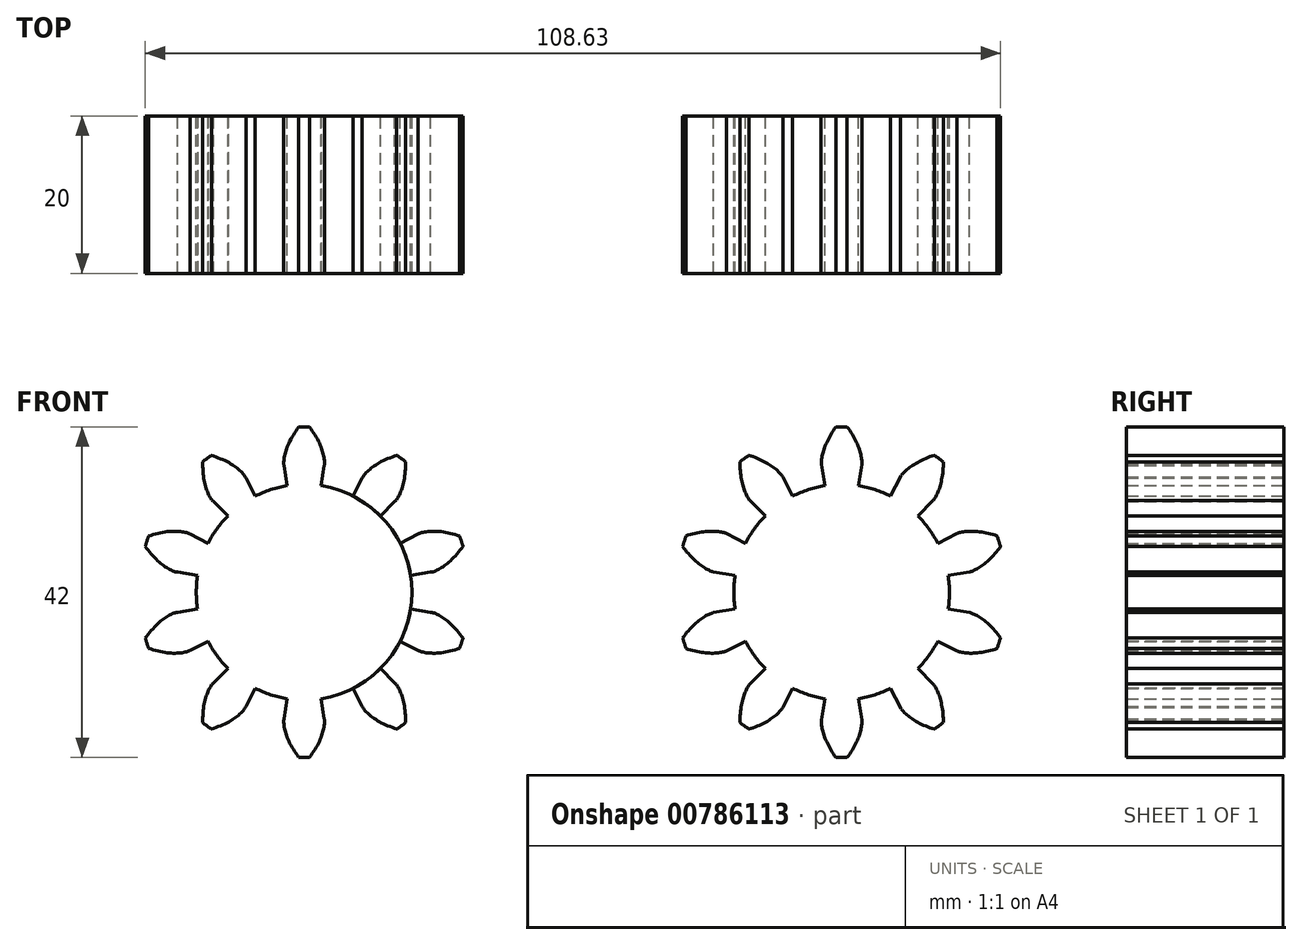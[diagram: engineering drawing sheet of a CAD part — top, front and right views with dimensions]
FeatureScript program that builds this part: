
annotation { "Feature Type Name" : "Feature", "Feature Type Description" : "" }
export const myFeature = defineFeature(function(context is Context, id is Id, definition is map)
    precondition{}
    {
        {
            var Q0;
            Q0=qCreatedBy(makeId("Front.planeOp"),FACE);
            var sketch = newSketch(context, id + "F0", { "sketchPlane" : qUnion([Q0])});
            skPoint(sketch, "E0.orphan", {"position": v(0, 0) * mm});
            skArc(sketch, "E1.0", {"start": v(0.7, 20.99) * mm, "mid": v(0, 21) * mm, "end": v(-0.7, 20.99) * mm});
            skArc(sketch, "E2.0", {"start": v(2.14, 13.53) * mm, "mid": v(0, 13.7) * mm, "end": v(-2.14, 13.53) * mm});
            skLineSegment(sketch, "E3", {"start": v(-2.14, 13.53) * mm, "end": v(-2.57, 16.24) * mm});
            skFitSpline(sketch, "E4", {"points": [v(-2.57, 16.24) * mm, v(-2.58, 16.45) * mm, v(-2.52, 17.07) * mm, v(-2.27, 18.07) * mm, v(-1.7, 19.4) * mm, v(-0.7, 20.99) * mm], "startDerivative": vector(-0.4, 1.4) * mm, "endDerivative": vector(3.94, 4.8) * mm});
            skLineSegment(sketch, "E5", {"start": v(-14.7, 0) * mm, "end": v(38.97, 0) * mm, "construction": true});
            skFitSpline(sketch, "E6.MirrorCS", {"points": [v(2.57, 16.24) * mm, v(2.58, 16.45) * mm, v(2.52, 17.07) * mm, v(2.27, 18.07) * mm, v(1.7, 19.4) * mm, v(0.7, 20.99) * mm], "startDerivative": vector(0.4, 1.4) * mm, "endDerivative": vector(-3.94, 4.8) * mm});
            skLineSegment(sketch, "E7.MirrorCS", {"start": v(2.14, 13.53) * mm, "end": v(2.57, 16.24) * mm});
            skSolve(sketch);
        }
        {
            var Q0;
            Q0=makeQuery(id+"F0.imprint","IMPRINT",FACE,{"disambiguationData":[TD([[makeQuery(id+"F0.imprint","IMPRINT",EDGE,{"derivedFrom":sQuery(id+"F0.wireOp",EDGE,"E1.0")}),1.0]])]});
            extrude(context, id + "F1", {"entities" : qUnion([Q0]), "depth" : 20 * mm, "offsetDistance" : 25 * mm});
        }
        {
            var Q0;
            Q0=qCreatedBy(makeId("Top.planeOp"),FACE);
            var sketch = newSketch(context, id + "F2", { "sketchPlane" : qUnion([Q0])});
            skLineSegment(sketch, "E8", {"start": v(0, 27.05) * mm, "end": v(0, -36.94) * mm, "construction": true});
            skSolve(sketch);
        }
        {
            var Q0;
            Q0=makeQuery(id+"F1.opExtrude","SWEPT_BODY",BODY,{"disambiguationData":[OSD([sQuery(id+"F0.wireOp",EDGE,"E1.0"),sQuery(id+"F0.wireOp",EDGE,"E2.0"),sQuery(id+"F0.wireOp",EDGE,"E3"),sQuery(id+"F0.wireOp",EDGE,"E4"),sQuery(id+"F0.wireOp",EDGE,"E6.MirrorCS"),sQuery(id+"F0.wireOp",EDGE,"E7.MirrorCS")])]});
            var Q1;
            Q1=sQuery(id+"F2.wireOp",EDGE,"E8");
            circularPattern(context, id + "F3", {"entities" : qUnion([Q0]), "axis" : qUnion([Q1]), "angle" : 360 * degree, "instanceCount" : 10, "equalSpace" : true});
        }
        {
            var Q0;
            Q0=qCreatedBy(makeId("Front.planeOp"),FACE);
            var sketch = newSketch(context, id + "F4", { "sketchPlane" : qUnion([Q0])});
            skCircle(sketch, "E9", {"center": v(0, 0) * mm, "radius": 13.7 * mm});
            skSolve(sketch);
        }
        {
            var Q0;
            Q0=makeQuery(id+"F4.imprint","IMPRINT",FACE,{"disambiguationData":[TD([[makeQuery(id+"F4.imprint","IMPRINT",EDGE,{"derivedFrom":sQuery(id+"F4.wireOp",EDGE,"E9")}),1.0]])]});
            extrude(context, id + "F5", {"entities" : qUnion([Q0]), "operationType" : NewBodyOperationType.ADD, "depth" : 20 * mm, "offsetDistance" : 25 * mm});
        }
        {
            var Q0;
            Q0=qCreatedBy(makeId("Front.planeOp"),FACE);
            var sketch = newSketch(context, id + "F6", { "sketchPlane" : qUnion([Q0])});
            skCircle(sketch, "E10", {"center": v(-68.27, 0) * mm, "radius": 13.7 * mm});
            skLineSegment(sketch, "E11", {"start": v(-70.82, 16.07) * mm, "end": v(-70.42, 13.53) * mm});
            skFitSpline(sketch, "E12", {"points": [v(-70.82, 16.07) * mm, v(-70.85, 16.27) * mm, v(-70.82, 16.9) * mm, v(-70.6, 17.9) * mm, v(-70.05, 19.25) * mm, v(-68.98, 20.99) * mm], "startDerivative": vector(-0.7, 1.8) * mm, "endDerivative": vector(3.56, 5.4) * mm});
            skFitSpline(sketch, "E13.MirrorCS", {"points": [v(-65.73, 16.07) * mm, v(-65.7, 16.27) * mm, v(-65.72, 16.9) * mm, v(-65.95, 17.9) * mm, v(-66.5, 19.25) * mm, v(-67.57, 20.99) * mm], "startDerivative": vector(0.7, 1.8) * mm, "endDerivative": vector(-3.56, 5.4) * mm});
            skLineSegment(sketch, "E14.MirrorCS", {"start": v(-65.73, 16.07) * mm, "end": v(-66.13, 13.53) * mm});
            skArc(sketch, "E15.trimOffspring", {"start": v(-67.57, 20.99) * mm, "mid": v(-68.27, 21) * mm, "end": v(-68.98, 20.99) * mm});
            skArc(sketch, "E16.trimOffspring", {"start": v(-66.13, 13.53) * mm, "mid": v(-68.27, 13.7) * mm, "end": v(-70.42, 13.53) * mm});
            skSolve(sketch);
        }
        {
            var Q0;
            {var subQ0=sQuery(id+"F6.wireOp",EDGE,"E11");Q0=makeQuery(id+"F6.imprint","IMPRINT",FACE,{"disambiguationData":[TD([[makeQuery(id+"F6.imprint","IMPRINT",EDGE,{"derivedFrom":subQ0}),1.0]])]});}
            extrude(context, id + "F7", {"entities" : qUnion([Q0]), "depth" : 20 * mm, "offsetDistance" : 25 * mm});
        }
        {
            var Q0;
            Q0=qCreatedBy(makeId("Top.planeOp"),FACE);
            var sketch = newSketch(context, id + "F8", { "sketchPlane" : qUnion([Q0])});
            skLineSegment(sketch, "E17", {"start": v(0, -32.15) * mm, "end": v(0, 21.31) * mm, "construction": true});
            skSolve(sketch);
        }
        {
            var Q0;
            Q0=qCreatedBy(makeId("Top.planeOp"),FACE);
            var sketch = newSketch(context, id + "F9", { "sketchPlane" : qUnion([Q0])});
            skLineSegment(sketch, "E18", {"start": v(-68.27, 16.24) * mm, "end": v(-68.27, -12.43) * mm});
            skSolve(sketch);
        }
        {
            var Q0;
            {var subQ0=sQuery(id+"F6.wireOp",EDGE,"E11");Q0=makeQuery(id+"F6.imprint","IMPRINT",FACE,{"disambiguationData":[TD([[makeQuery(id+"F6.imprint","IMPRINT",EDGE,{"derivedFrom":subQ0}),1.0]])]});}
            extrude(context, id + "F10", {"entities" : qUnion([Q0]), "depth" : 20 * mm, "offsetDistance" : 25 * mm});
        }
        {
            var Q0;
            Q0=makeQuery(id+"F10.opExtrude","SWEPT_BODY",BODY,{"disambiguationData":[OSD([sQuery(id+"F6.wireOp",EDGE,"E10"),sQuery(id+"F6.wireOp",EDGE,"E11"),sQuery(id+"F6.wireOp",EDGE,"E12"),sQuery(id+"F6.wireOp",EDGE,"E13.MirrorCS"),sQuery(id+"F6.wireOp",EDGE,"E14.MirrorCS"),sQuery(id+"F6.wireOp",EDGE,"E15.trimOffspring")])]});
            var Q1;
            Q1=sQuery(id+"F9.wireOp",EDGE,"E18");
            circularPattern(context, id + "F11", {"entities" : qUnion([Q0]), "axis" : qUnion([Q1]), "angle" : 360 * degree, "instanceCount" : 10, "equalSpace" : true});
        }
        {
            var Q0;
            {var subQ0=sQuery(id+"F6.wireOp",EDGE,"E10");var subQ1=makeQuery(id+"F6.imprint","INTERSECT",VERTEX,{"derivedFrom":[subQ0,sQuery(id+"F6.wireOp",EDGE,"E11")]});Q0=makeQuery(id+"F6.imprint","IMPRINT",FACE,{"disambiguationData":[TD([[makeQuery(id+"F6.imprint","IMPRINT",EDGE,{"disambiguationData":[TD([[subQ1,1.0]])],"derivedFrom":subQ0}),1.0]])]});}
            extrude(context, id + "F12", {"entities" : qUnion([Q0]), "operationType" : NewBodyOperationType.ADD, "depth" : 20 * mm, "offsetDistance" : 25 * mm});
        }
    });
